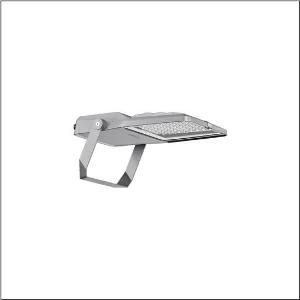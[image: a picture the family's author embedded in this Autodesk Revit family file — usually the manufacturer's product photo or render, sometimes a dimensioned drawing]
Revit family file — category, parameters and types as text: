
# Revit family: floodlight_fl_21_iq_mini___pl64_5xa7772c2e1a_df54
name_source: partatom
category: Lighting Fixtures
units: mm (PartAtom-declared; Revit-internal decimal feet)

## family parameters
Cut with Voids When Loaded = No
Host = Face
Light Source = No
Part Type = Normal
Room Calculation Point = No
Round Connector Dimension = Use Diameter
Shared = No

## types (1)
- --- (1 x LED, 11790 lm, 87.2 W, 3000K)
    Apparent Load = 87 VA
    CIE Flux Codes = 28 80 98 100 100
    Color Rendering = 70
    Color Temperature = 3000K
    Default Elevation = 1800 mm
    Description = Floodlight FL 21 iQ mini, floodlight, primary light control with lens, of PMMA, primary optical cover: protective disc, of toughened safety glass, transparent, light distribution: PL64, light emission: direct distribution, installation type: surface-mounted, LED, High Power LED, rated luminous flux: 11.790lm, luminous efficacy: 135lm/W, light colour: 730, colour temperature: 3000K, control: Street-Remote, Auto-Match, Temp-Guard, Night-Set, Smart-Wire, Desk-Remote (wireless, voltage-free reading and setting of iQ features in the workshop via application-optimized NFC function/RFID function), optimised constant luminous flux control (CLO 2.0), with terminal, 6-pole, mains connection: 220..240V, AC, 50/60Hz, start of lifetime: 87W, end of service life: 92W, reduction: 40W, luminaire housing, of diecast aluminium, powder-coated, Siteco® metallic grey (DB 702S), corrosivity category C5 mid according to DIN EN ISO 12944, sealing non-destructively replaceable, mounting bracket, of steel, galvanised, powder-coated, Siteco® metallic grey (DB 702S), protection rating (complete): IP66, insulation class (complete): insulation class II (safety insulation), certification: CE, ENEC, VDE, protection symbol: D, impact resistance: IK08, permissible operating ambient temperature: -40..+40°C, permissible operating ambient temperature for outdoor applications: -40..+50°C, standard: DIN EN 12944, LABS conformity tested according to VDMA 24364:2018-05, packaging unit: 1 piece

Light Distribution: PL64
    Height = 70 mm
    Lamp = 1 x LED
    Lamp Light Flux = 11790 lm
    Lamp Power = 87.2 W
    Lamp count = 1
    Length = 485 mm
    Luminous efficacy = 135 lm/W
    Manufacturer = Siteco
    ModVariant = No
    Model = 5XA7772C2E1A
    Number of Poles = 1
    OnlyDefault = Yes
    Power Factor = 1
    Product Name = Floodlight FL 21 iQ mini | PL64
    Product group = floodlight | pylon annexe
    ProductGroupID = 6200
    Protection Class = Protection class II
    Protection Degree = IP 66
    RLX_Detail_Level = 1
    RLX_Emergency_Light_Flux = 0 lm
    RLX_Emergency_Type = 0
    RLX_Emergency_Type_DB = No
    RlxData = <blob elided: 96429 chars, md5=ddfa9558>
    Socket = socket
    Standby Power = 0 W
    System Light Flux = 11790 lm
    System Power = 87 W
    Type Comments = factory setting: luminous flux: 100 % | dim-lin: 254 | 456 mA
    Type Image = l_1006845.jpg
    URL = http://relux.com
    VarID = @adj_098733
    Voltage = 0 V
    Weight = 0.00 kg
    Width = 337 mm

## geometry (parser evidence)
native form markers: Blend x4, Sweep x11
no freeform markers — native parametric forms only
